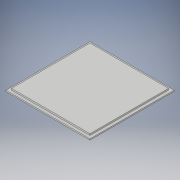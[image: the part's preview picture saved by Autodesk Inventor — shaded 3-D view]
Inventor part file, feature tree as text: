
AUTODESK INVENTOR PART (.ipt)
format: ipt  version: 2018.3 (Build 223284000, 284)  size: 112,640 bytes
history: native  units: mm
features: extrude x2, sketch x2, plane x1, projected_geometry x1
ambient origin geometry x8: Origin, YZ Plane, XZ Plane, XY Plane, X Axis, Y Axis, Z Axis, Center Point
bodies: Body1 (feature_tree)
feature tree (6):
  plane  "Arbeitsebene3"
  extrude  "Extrusion2"  Depth=540.0mm
  extrude  "Extrusion3"  Depth=18.0mm
  sketch  "Skizze2"  dims[d5=540.0mm d6=540.0mm]
  sketch  "Skizze3"  dims[d7=18.0mm d8=0.0mm d12=18.0mm d13=18.0mm d14=18.0mm d15=18.0mm d16=10.0mm d17=0.0mm]
  projected_geometry  "Projizierte Kontur1"
